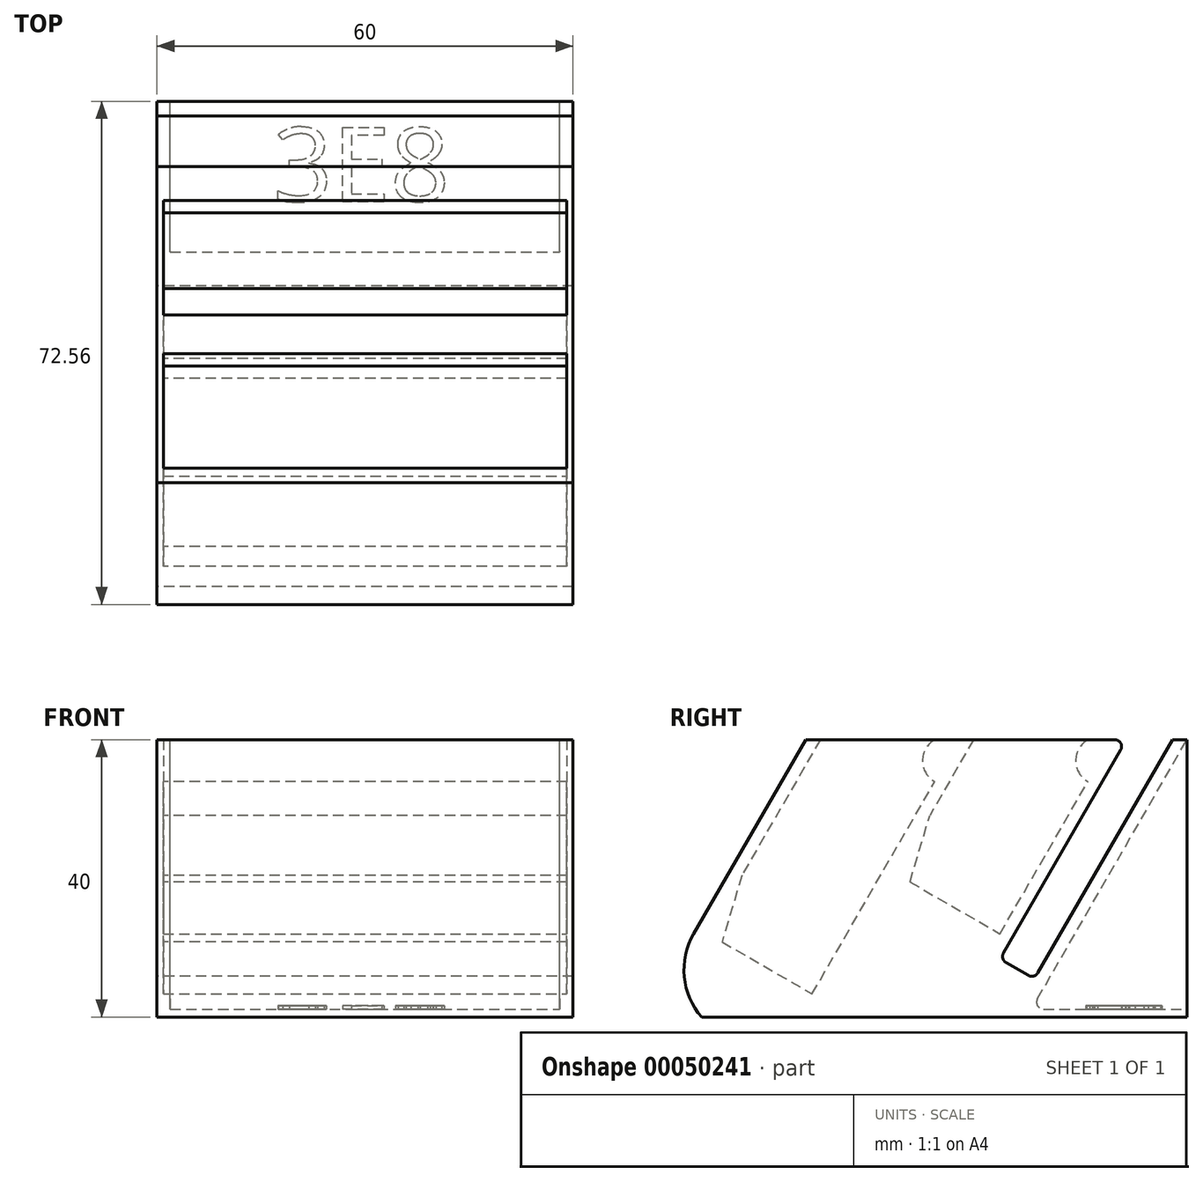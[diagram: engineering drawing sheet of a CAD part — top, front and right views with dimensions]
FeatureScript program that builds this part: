
annotation { "Feature Type Name" : "Feature", "Feature Type Description" : "" }
export const myFeature = defineFeature(function(context is Context, id is Id, definition is map)
    precondition{}
    {
        {
            var Q0;
            Q0=qCreatedBy(makeId("Right.planeOp"),FACE);
            var sketch = newSketch(context, id + "F0", { "sketchPlane" : qUnion([Q0])});
            skLineSegment(sketch, "E0", {"start": v(-35, 0) * mm, "end": v(35, 0) * mm});
            skLineSegment(sketch, "E1", {"start": v(35, 0) * mm, "end": v(35, 40) * mm});
            skLineSegment(sketch, "E2", {"start": v(35, 40) * mm, "end": v(-20, 40) * mm});
            skLineSegment(sketch, "E3", {"start": v(-20, 40) * mm, "end": v(-36.17, 11.99) * mm});
            skArc(sketch, "E4", {"start": v(-36.17, 11.99) * mm, "mid": v(-37.51, 5.8) * mm, "end": v(-35, 0) * mm});
            skSolve(sketch);
        }
        {
            var Q0;
            Q0=makeQuery(id+"F0.imprint","IMPRINT",FACE,{"disambiguationData":[TD([[makeQuery(id+"F0.imprint","IMPRINT",EDGE,{"derivedFrom":sQuery(id+"F0.wireOp",EDGE,"E0")}),1.0]])]});
            extrude(context, id + "F1", {"entities" : qUnion([Q0]), "endBound" : BoundingType.SYMMETRIC, "depth" : 60 * mm});
        }
        {
            var Q0;
            Q0=makeQuery(id+"F1.opExtrude","CAP_FACE",FACE,{"disambiguationData":[OSD([sQuery(id+"F0.wireOp",EDGE,"E0"),sQuery(id+"F0.wireOp",EDGE,"E1"),sQuery(id+"F0.wireOp",EDGE,"E2"),sQuery(id+"F0.wireOp",EDGE,"E3"),sQuery(id+"F0.wireOp",EDGE,"E4")])],"isStart":false});
            cPlane(context, id + "F2", {"entities" : qUnion([Q0]), "cplaneType" : CPlaneType.OFFSET, "offset" : .9 * mm, "oppositeDirection" : true, "width" : 150 * mm, "height" : 150 * mm});
        }
        {
            var Q0;
            Q0=qCreatedBy(id+"F2.planeOp",FACE);
            var sketch = newSketch(context, id + "F3", { "sketchPlane" : qUnion([Q0])});
            skPoint(sketch, "E5", {"position": v(-20, 40) * mm});
            skPoint(sketch, "E6", {"position": v(35, 0) * mm});
            skPoint(sketch, "E7", {"position": v(-35, 0) * mm});
            skPoint(sketch, "E8", {"position": v(-36.17, 11.99) * mm});
            skLineSegment(sketch, "E9", {"start": v(-20, 40) * mm, "end": v(-17.9, 40) * mm, "construction": true});
            skLineSegment(sketch, "E10", {"start": v(-36.17, 11.99) * mm, "end": v(-34.07, 11.99) * mm, "construction": true});
            skLineSegment(sketch, "E11", {"start": v(26.3, 40) * mm, "end": v(24.2, 40) * mm, "construction": true});
            skLineSegment(sketch, "E12", {"start": v(-17.9, 40) * mm, "end": v(-34.07, 11.99) * mm});
            skLineSegment(sketch, "E13", {"start": v(-34.07, 11.99) * mm, "end": v(-19.07, 3.33) * mm});
            skLineSegment(sketch, "E14", {"start": v(-19.07, 3.33) * mm, "end": v(2.1, 40) * mm});
            skLineSegment(sketch, "E15", {"start": v(2.1, 40) * mm, "end": v(4.2, 40) * mm, "construction": true});
            skLineSegment(sketch, "E16", {"start": v(12.57, 1.15) * mm, "end": v(35, 40) * mm});
            skLineSegment(sketch, "E17", {"start": v(4.2, 40) * mm, "end": v(24.2, 40) * mm});
            skLineSegment(sketch, "E18", {"start": v(-17.9, 40) * mm, "end": v(2.1, 40) * mm});
            skLineSegment(sketch, "E19", {"start": v(12.57, 1.15) * mm, "end": v(35, 1.15) * mm});
            skLineSegment(sketch, "E20", {"start": v(35, 1.15) * mm, "end": v(35, 40) * mm});
            skLineSegment(sketch, "E21", {"start": v(-34.07, 11.99) * mm, "end": v(8.03, 11.99) * mm, "construction": true});
            skLineSegment(sketch, "E22", {"start": v(4.2, 40) * mm, "end": v(-6.97, 20.65) * mm});
            skLineSegment(sketch, "E23", {"start": v(-6.97, 20.65) * mm, "end": v(8.03, 11.99) * mm});
            skLineSegment(sketch, "E24", {"start": v(8.03, 11.99) * mm, "end": v(24.2, 40) * mm});
            skSolve(sketch);
        }
        {
            var Q0;
            Q0 = qSketchRegion(id + "F3", true);
            extrude(context, id + "F4", {"entities" : qUnion([Q0]), "operationType" : NewBodyOperationType.REMOVE, "oppositeDirection" : true, "depth" : 58.2 * mm});
        }
        {
            var Q0;
            Q0=makeQuery(id+"F4.boolean.opBoolean","COPY",FACE,{"derivedFrom":makeQuery(id+"F4.opExtrude","CAP_FACE",FACE,{"disambiguationData":[OSD([sQuery(id+"F3.wireOp",EDGE,"be90a4c1-fdc4-44e3-ab6c-95068b80fabc"),sQuery(id+"F3.wireOp",EDGE,"26c6214a-6b9a-4307-9401-254e5f0091ab"),sQuery(id+"F3.wireOp",EDGE,"35e6dab0-42ec-4566-bf5d-57dbf1a0a791"),sQuery(id+"F3.wireOp",EDGE,"E16")])],"isStart":true})});
            extrude(context, id + "F5", {"entities" : qUnion([Q0]), "operationType" : NewBodyOperationType.ADD, "depth" : 1 * mm});
        }
        {
            var Q0;
            Q0=makeQuery(id+"F4.boolean.opBoolean","COPY",FACE,{"derivedFrom":makeQuery(id+"F4.opExtrude","CAP_FACE",FACE,{"disambiguationData":[OSD([sQuery(id+"F3.wireOp",EDGE,"be90a4c1-fdc4-44e3-ab6c-95068b80fabc"),sQuery(id+"F3.wireOp",EDGE,"26c6214a-6b9a-4307-9401-254e5f0091ab"),sQuery(id+"F3.wireOp",EDGE,"35e6dab0-42ec-4566-bf5d-57dbf1a0a791"),sQuery(id+"F3.wireOp",EDGE,"E16")])],"isStart":false})});
            extrude(context, id + "F6", {"entities" : qUnion([Q0]), "operationType" : NewBodyOperationType.ADD, "depth" : 1 * mm});
        }
        {
            var Q0;
            Q0=makeQuery(id+"F4.boolean.opBoolean","COPY",FACE,{"derivedFrom":makeQuery(id+"F4.opExtrude","SWEPT_FACE",FACE,{"disambiguationData":[OSD([sQuery(id+"F3.wireOp",EDGE,"E19")])]})});
            var sketch = newSketch(context, id + "F7", { "sketchPlane" : qUnion([Q0])});
            skText(sketch, "E25", { "text": "3E8", "fontName": "OpenSans-Regular.ttf"});
            const initialGuessF7  = {"E25": [-0.01326, 0.02053, 1, 0, 0.01078]};
            skSetInitialGuess(sketch, initialGuessF7);
            skSolve(sketch);
        }
        {
            var Q0;
            Q0 = qSketchRegion(id + "F7", true);
            extrude(context, id + "F8", {"entities" : qUnion([Q0]), "operationType" : NewBodyOperationType.ADD, "depth" : .5 * mm});
        }
        {
            var Q0;
            Q0=makeQuery(id+"F1.opExtrude","CAP_FACE",FACE,{"disambiguationData":[OSD([sQuery(id+"F0.wireOp",EDGE,"E0"),sQuery(id+"F0.wireOp",EDGE,"E1"),sQuery(id+"F0.wireOp",EDGE,"E2"),sQuery(id+"F0.wireOp",EDGE,"E3"),sQuery(id+"F0.wireOp",EDGE,"E4")])],"isStart":false});
            var sketch = newSketch(context, id + "F9", { "sketchPlane" : qUnion([Q0])});
            skPoint(sketch, "E26.0", {"position": v(26.3, 40) * mm});
            skLineSegment(sketch, "E27", {"start": v(26.3, 40) * mm, "end": v(8.03, 8.35) * mm});
            skLineSegment(sketch, "E28", {"start": v(8.03, 8.35) * mm, "end": v(12.98, 5.5) * mm});
            skLineSegment(sketch, "E29", {"start": v(12.98, 5.5) * mm, "end": v(32.9, 40) * mm});
            skLineSegment(sketch, "E30", {"start": v(32.9, 40) * mm, "end": v(26.3, 40) * mm});
            skLineSegment(sketch, "E31", {"start": v(35, 40) * mm, "end": v(32.9, 40) * mm, "construction": true});
            skLineSegment(sketch, "E32.0", {"start": v(8.03, 11.99) * mm, "end": v(24.2, 40) * mm, "construction": true});
            skLineSegment(sketch, "E33", {"start": v(8.03, 11.99) * mm, "end": v(8.03, 8.35) * mm, "construction": true});
            skLineSegment(sketch, "E34.0", {"start": v(-6.97, 20.65) * mm, "end": v(8.03, 11.99) * mm, "construction": true});
            skLineSegment(sketch, "E35", {"start": v(0.53, 16.32) * mm, "end": v(-3.47, 9.39) * mm, "construction": true});
            skCircle(sketch, "E36", {"center": v(-3.47, 9.39) * mm, "radius": 2.5 * mm, "construction": true});
            skLineSegment(sketch, "E37.0", {"start": v(-34.07, 11.99) * mm, "end": v(-19.07, 3.33) * mm, "construction": true});
            skLineSegment(sketch, "E38", {"start": v(-26.57, 7.66) * mm, "end": v(-28.57, 4.2) * mm, "construction": true});
            skCircle(sketch, "E39", {"center": v(-28.57, 4.2) * mm, "radius": 2.5 * mm, "construction": true});
            skSolve(sketch);
        }
        {
            var Q0;
            Q0=makeQuery(id+"F9.imprint","IMPRINT",FACE,{"disambiguationData":[TD([[makeQuery(id+"F9.imprint","IMPRINT",EDGE,{"derivedFrom":sQuery(id+"F9.wireOp",EDGE,"E36")}),1.0]])]});
            var Q1;
            Q1=makeQuery(id+"F9.imprint","IMPRINT",FACE,{"disambiguationData":[TD([[makeQuery(id+"F9.imprint","IMPRINT",EDGE,{"derivedFrom":sQuery(id+"F9.wireOp",EDGE,"E27")}),1.0]])]});
            var Q2;
            Q2=makeQuery(id+"F9.imprint","IMPRINT",FACE,{"disambiguationData":[TD([[makeQuery(id+"F9.imprint","IMPRINT",EDGE,{"derivedFrom":sQuery(id+"F9.wireOp",EDGE,"E39")}),1.0]])]});
            var Q3;
            Q3 = qConstructionFilter(qBodyType(qCreatedBy(id + "F9" ,EDGE), BodyType.WIRE), ConstructionObject.NO);
            extrude(context, id + "F10", {"entities" : qUnion([Q0, Q1, Q2]), "operationType" : NewBodyOperationType.REMOVE, "surfaceEntities" : qUnion([Q3]), "endBound" : BoundingType.THROUGH_ALL, "oppositeDirection" : true, "depth" : 25 * mm});
        }
        {
            var Q0;
            Q0=makeQuery(id+"F10.boolean.opBoolean","COPY",EDGE,{"derivedFrom":makeQuery(id+"F10.opExtrude","SWEPT_EDGE",EDGE,{"disambiguationData":[OSD([sQuery(id+"F0.wireOp",EDGE,"E2"),sQuery(id+"F9.wireOp",EDGE,"E29"),sQuery(id+"F9.wireOp",EDGE,"E30")])]})});
            var Q1;
            Q1=makeQuery(id+"F10.boolean.opBoolean","COPY",EDGE,{"derivedFrom":makeQuery(id+"F10.opExtrude","SWEPT_EDGE",EDGE,{"disambiguationData":[OSD([sQuery(id+"F0.wireOp",EDGE,"E2"),sQuery(id+"F9.wireOp",EDGE,"E27"),sQuery(id+"F9.wireOp",EDGE,"E30")])]})});
            var Q2;
            Q2=makeQuery(id+"F10.boolean.opBoolean","COPY",EDGE,{"derivedFrom":makeQuery(id+"F10.opExtrude","SWEPT_EDGE",EDGE,{"disambiguationData":[OSD([sQuery(id+"F9.wireOp",EDGE,"E27"),sQuery(id+"F9.wireOp",EDGE,"E28")])]})});
            var Q3;
            Q3=makeQuery(id+"F10.boolean.opBoolean","COPY",EDGE,{"derivedFrom":makeQuery(id+"F10.opExtrude","SWEPT_EDGE",EDGE,{"disambiguationData":[OSD([sQuery(id+"F9.wireOp",EDGE,"E28"),sQuery(id+"F9.wireOp",EDGE,"E29")])]})});
            var Q4;
            Q4=makeQuery(id+"F4.boolean.opBoolean","COPY",EDGE,{"derivedFrom":makeQuery(id+"F4.opExtrude","SWEPT_EDGE",EDGE,{"disambiguationData":[OSD([sQuery(id+"F3.wireOp",EDGE,"E16"),sQuery(id+"F3.wireOp",EDGE,"E19")])]})});
            fillet(context, id + "F11", {"entities" : qUnion([Q0, Q1, Q2, Q3, Q4]), "radius" : 1 * mm, "tangentPropagation" : true, "allowEdgeOverflow" : false});
        }
        {
            var Q0;
            Q0=makeQuery(id+"F4.boolean.opBoolean","COPY",FACE,{"derivedFrom":makeQuery(id+"F4.opExtrude","CAP_FACE",FACE,{"disambiguationData":[OSD([sQuery(id+"F3.wireOp",EDGE,"E17"),sQuery(id+"F3.wireOp",EDGE,"E22"),sQuery(id+"F3.wireOp",EDGE,"E23"),sQuery(id+"F3.wireOp",EDGE,"E24")])],"isStart":false})});
            var sketch = newSketch(context, id + "F12", { "sketchPlane" : qUnion([Q0])});
            skLineSegment(sketch, "E40", {"start": v(24.2, 40) * mm, "end": v(20.7, 33.94) * mm});
            skArc(sketch, "E41", {"start": v(24.2, 40) * mm, "mid": v(19.42, 38.72) * mm, "end": v(20.7, 33.94) * mm});
            skPoint(sketch, "E42.0", {"position": v(2.1, 40) * mm});
            skLineSegment(sketch, "E43.0", {"start": v(-19.07, 3.33) * mm, "end": v(2.1, 40) * mm, "construction": true});
            skLineSegment(sketch, "E44", {"start": v(2.1, 40) * mm, "end": v(-1.4, 33.94) * mm});
            skArc(sketch, "E45", {"start": v(2.1, 40) * mm, "mid": v(-2.68, 38.72) * mm, "end": v(-1.4, 33.94) * mm});
            skLineSegment(sketch, "E46.0", {"start": v(-17.9, 40) * mm, "end": v(2.1, 40) * mm});
            skLineSegment(sketch, "E47.0", {"start": v(4.2, 40) * mm, "end": v(24.2, 40) * mm});
            skLineSegment(sketch, "E48", {"start": v(8.03, 11.99) * mm, "end": v(-4.96, 19.49) * mm, "construction": true});
            skLineSegment(sketch, "E49", {"start": v(-4.96, 19.49) * mm, "end": v(-2.1, 29.07) * mm});
            skLineSegment(sketch, "E50", {"start": v(-2.1, 29.07) * mm, "end": v(-6.97, 20.65) * mm});
            skLineSegment(sketch, "E51", {"start": v(-6.97, 20.65) * mm, "end": v(-4.96, 19.49) * mm});
            skPoint(sketch, "E52.0", {"position": v(-34.07, 11.99) * mm});
            skLineSegment(sketch, "E53", {"start": v(-19.07, 3.33) * mm, "end": v(-32.06, 10.83) * mm, "construction": true});
            skLineSegment(sketch, "E54", {"start": v(-32.06, 10.83) * mm, "end": v(-34.07, 11.99) * mm});
            skLineSegment(sketch, "E55", {"start": v(-34.07, 11.99) * mm, "end": v(-29.2, 20.41) * mm});
            skLineSegment(sketch, "E56", {"start": v(-29.2, 20.41) * mm, "end": v(-32.06, 10.83) * mm});
            skSolve(sketch);
        }
        {
            var Q0;
            {var subQ0=sQuery(id+"F12.wireOp",EDGE,"E44");Q0=makeQuery(id+"F12.imprint","IMPRINT",FACE,{"disambiguationData":[TD([[makeQuery(id+"F12.imprint","IMPRINT",EDGE,{"derivedFrom":subQ0}),-1.0]])]});}
            var Q1;
            {var subQ0=sQuery(id+"F12.wireOp",EDGE,"E40");Q1=makeQuery(id+"F12.imprint","IMPRINT",FACE,{"disambiguationData":[TD([[makeQuery(id+"F12.imprint","IMPRINT",EDGE,{"derivedFrom":subQ0}),1.0]])]});}
            var Q2;
            Q2=makeQuery(id+"F12.imprint","IMPRINT",FACE,{"disambiguationData":[TD([[makeQuery(id+"F12.imprint","IMPRINT",EDGE,{"derivedFrom":sQuery(id+"F12.wireOp",EDGE,"E49")}),1.0]])]});
            var Q3;
            Q3=makeQuery(id+"F12.imprint","IMPRINT",FACE,{"disambiguationData":[TD([[makeQuery(id+"F12.imprint","IMPRINT",EDGE,{"derivedFrom":sQuery(id+"F12.wireOp",EDGE,"E54")}),-1.0]])]});
            extrude(context, id + "F13", {"entities" : qUnion([Q0, Q1, Q2, Q3]), "operationType" : NewBodyOperationType.ADD, "endBound" : BoundingType.UP_TO_NEXT, "depth" : 25 * mm});
        }
    });
